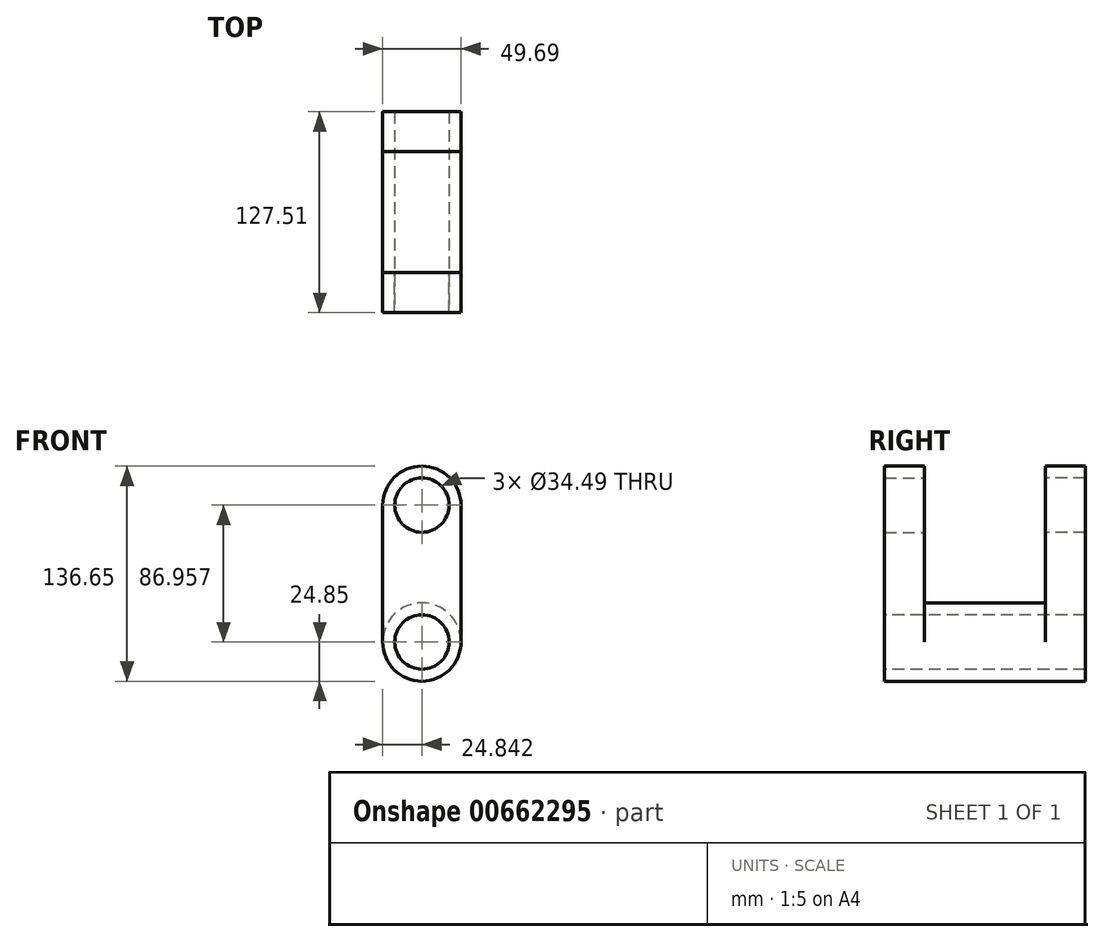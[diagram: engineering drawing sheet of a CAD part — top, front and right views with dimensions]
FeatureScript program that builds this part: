
annotation { "Feature Type Name" : "Feature", "Feature Type Description" : "" }
export const myFeature = defineFeature(function(context is Context, id is Id, definition is map)
    precondition{}
    {
        {
            var Q0;
            Q0=qCreatedBy(makeId("Front.planeOp"),FACE);
            var sketch = newSketch(context, id + "F0", { "sketchPlane" : qUnion([Q0])});
            skPoint(sketch, "E0.center.orphan", {"position": v(4.71, 26.99) * mm});
            skLineSegment(sketch, "E1", {"start": v(-20.13, 26.99) * mm, "end": v(-20.13, -59.97) * mm});
            skLineSegment(sketch, "E2", {"start": v(29.56, 26.99) * mm, "end": v(29.56, -59.97) * mm});
            skCircle(sketch, "E3", {"center": v(4.71, -59.97) * mm, "radius": 24.84 * mm});
            skCircle(sketch, "E4", {"center": v(4.71, 26.99) * mm, "radius": 24.84 * mm});
            skPoint(sketch, "E5.orphan", {"position": v(29.56, -60.11) * mm});
            skPoint(sketch, "E6.orphan", {"position": v(-20.13, -59.83) * mm});
            skPoint(sketch, "E7.orphan", {"position": v(29.56, 26.99) * mm});
            skPoint(sketch, "E8.orphan", {"position": v(-20.13, 26.99) * mm});
            skCircle(sketch, "E9", {"center": v(4.71, 26.99) * mm, "radius": 17.24 * mm});
            skCircle(sketch, "E10", {"center": v(4.71, -59.97) * mm, "radius": 17.24 * mm});
            skSolve(sketch);
        }
        {
            var Q0;
            Q0=makeQuery(id+"F0.imprint","IMPRINT",FACE,{"disambiguationData":[TD([[makeQuery(id+"F0.imprint","IMPRINT",EDGE,{"derivedFrom":sQuery(id+"F0.wireOp",EDGE,"E10")}),-1.0]])]});
            var Q1;
            {var subQ0=sQuery(id+"F0.wireOp",EDGE,"E1");Q1=makeQuery(id+"F0.imprint","IMPRINT",FACE,{"disambiguationData":[TD([[makeQuery(id+"F0.imprint","IMPRINT",EDGE,{"derivedFrom":subQ0}),1.0]])]});}
            var Q2;
            Q2=makeQuery(id+"F0.imprint","IMPRINT",FACE,{"disambiguationData":[TD([[makeQuery(id+"F0.imprint","IMPRINT",EDGE,{"derivedFrom":sQuery(id+"F0.wireOp",EDGE,"E9")}),-1.0]])]});
            extrude(context, id + "F1", {"entities" : qUnion([Q0, Q1, Q2]), "oppositeDirection" : true, "depth" : 25.4 * mm, "offsetDistance" : 25.4 * mm});
        }
        {
            var Q0;
            Q0=makeQuery(id+"F0.imprint","IMPRINT",FACE,{"disambiguationData":[TD([[makeQuery(id+"F0.imprint","IMPRINT",EDGE,{"derivedFrom":sQuery(id+"F0.wireOp",EDGE,"E10")}),-1.0]])]});
            extrude(context, id + "F2", {"entities" : qUnion([Q0]), "operationType" : NewBodyOperationType.ADD, "depth" : 38.35 * mm, "offsetDistance" : 25.4 * mm});
        }
        {
            var Q0;
            Q0=makeQuery(id+"F1.opExtrude","SWEPT_BODY",BODY,{"disambiguationData":[OSD([sQuery(id+"F0.wireOp",EDGE,"E1"),sQuery(id+"F0.wireOp",EDGE,"E2"),sQuery(id+"F0.wireOp",EDGE,"E3"),sQuery(id+"F0.wireOp",EDGE,"E4"),sQuery(id+"F0.wireOp",EDGE,"E9"),sQuery(id+"F0.wireOp",EDGE,"E10")])]});
            var Q1;
            Q1=makeQuery(id+"F2.opExtrude","CAP_FACE",FACE,{"disambiguationData":[OSD([sQuery(id+"F0.wireOp",EDGE,"E3"),sQuery(id+"F0.wireOp",EDGE,"E10")])],"isStart":false});
            mirror(context, id + "F3", {"operationType" : NewBodyOperationType.ADD, "entities" : qUnion([Q0]), "mirrorPlane" : qUnion([Q1])});
        }
    });
